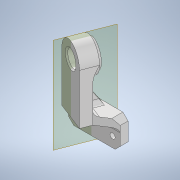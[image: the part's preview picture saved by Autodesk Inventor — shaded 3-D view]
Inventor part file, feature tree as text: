
AUTODESK INVENTOR PART (.ipt)
format: ipt  version: 2023 (Build 270158000, 158)  size: 367,104 bytes
history: native  units: mm
features: extrude x13, sketch x13, projected_geometry x13, other x5, chamfer x4, fillet x3, reference x3, plane x1
ambient origin geometry x8: Origin, YZ Plane, XZ Plane, XY Plane, X Axis, Y Axis, Z Axis, Center Point
bodies: Solid1 (feature_tree)
feature tree (55):
  extrude  "Extrusion1"  Depth=8.0mm
  extrude  "Extrusion2"  Depth=2.0mm
  extrude  "Extrusion3"  Depth=20.0mm
  extrude  "Extrusion5"  Depth=3.0mm
  extrude  "Extrusion6"  Depth=3.0mm
  extrude  "Extrusion7"  Depth=1.0mm
  extrude  "Extrusion8"  Depth=25.0mm TaperAngle=0.0deg
  extrude  "Extrusion10"  Depth=6.0mm
  extrude  "Extrusion11"  Depth=6.0mm
  plane  "Work Plane1"
  extrude  "Extrusion12"  Depth=4.5mm
  fillet  "Fillet1"  Radius=25.0mm
  fillet  "Fillet2"  Radius=25.0mm
  chamfer  "Chamfer1"  Distance=25.0mm
  chamfer  "Chamfer2"  Distance=25.0mm
  extrude  "Extrusion13"  Depth=6.0mm
  extrude  "Extrusion14"  Depth=2.0mm TaperAngle=0.0deg
  extrude  "Extrusion15"  Depth=2.0mm
  fillet  "Fillet3"  Radius=1.5mm
  chamfer  "Chamfer4"  Distance=2.0mm Angle=45.0deg
  chamfer  "Chamfer5"  Distance=2.0mm Angle=45.0deg
  sketch  "Sketch1"  dims[d0=8.0mm d1=20.0mm]
  reference  "Reference1"
  sketch  "Sketch2"  dims[d2=2.0mm d3=2.0mm]
  projected_geometry  "Projected Loop1"
  reference  "Reference2"
  sketch  "Sketch3"  dims[d4=3.0mm d5=0.0mm d6=20.0mm]
  projected_geometry  "Projected Loop2"
  sketch  "Sketch4"  dims[d7=3.0mm d8=3.0mm]
  reference  "Reference3"
  sketch  "Sketch5"  dims[d9=3.0mm d10=3.0mm]
  projected_geometry  "Projected Loop3"
  sketch  "Sketch6"  dims[d11=3.0mm d12=0.0mm d13=1.0mm]
  projected_geometry  "Projected Loop4"
  sketch  "Sketch7"  dims[d14=14.0mm d15=25.0mm d16=0.0mm]
  projected_geometry  "Projected Loop5"
  sketch  "Sketch9"  dims[d17=6.0mm d20=3.0mm]
  projected_geometry  "Projected Loop7"
  sketch  "Sketch10"  dims[d21=25.0mm d22=0.0mm d23=6.0mm]
  projected_geometry  "Projected Loop8"
  sketch  "Sketch11"  dims[d24=25.0mm d25=0.0mm d26=4.5mm d27=25.0mm d28=0.0mm d29=25.0mm d30=0.0mm]
  projected_geometry  "Projected Loop9"
  projected_geometry  "Projected Loop10"
  sketch  "Sketch12"  dims[d34=6.0mm d35=25.0mm d36=0.0mm d37=25.0mm d38=0.0mm]
  projected_geometry  "Projected Loop11"
  sketch  "Sketch13"  dims[d39=6.0mm d40=3.0mm]
  projected_geometry  "Projected Loop12"
  projected_geometry  "Projected Loop13"
  projected_geometry  "Projected Loop14"
  sketch  "Sketch14"  dims[d41=5.0mm d42=2.0mm d43=0.0mm d44=1.5mm d45=1.5mm d46=2.0mm d47=2.0mm d48=45.0deg d49=2.0mm d50=2.0mm d51=45.0deg d52=12.0mm d53=3.0mm d54=0.0mm d55=8.0mm d56=0.0mm d60=6.15mm d61=10.0mm d62=0.0mm d63=2.0mm d64=1.0mm d65=2.0mm d66=45.0deg d67=0.5mm d68=2.0mm d69=45.0deg]
  parser-record x1  (decoder bookkeeping rows leaked as tree rows — omitted from the tree; the rows remain in map.json)
  other  "body_1.iam"
  other  "leg_1:1"
  other  "leg_holder_2:1"
  other  "body_conn_1:1"
note: 1 file-system path scrubbed to <path> (originals preserved in map.json)
